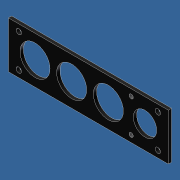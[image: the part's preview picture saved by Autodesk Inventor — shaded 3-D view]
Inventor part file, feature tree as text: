
AUTODESK INVENTOR PART (.ipt)
format: ipt  version: unknown  size: 224,256 bytes
history: native  units: in
note: dims shown in document units (in); Inventor stores cm internally (conversion verified against a paired STEP export)
features: sketch x5, extrude x3, hole x2, reference x2
ambient origin geometry x8: Origin, YZ Plane, XZ Plane, XY Plane, X Axis, Y Axis, Z Axis, Center Point
bodies: Solid1 (feature_tree)
feature tree (12):
  extrude  "Extrusion1"  Depth=1.75in
  extrude  "Extrusion2"  Depth=1.125in
  hole  "Hole1"  [1 undecoded]
  hole  "Hole2"  [1 undecoded]
  extrude  "Extrusion3"  Depth=0.25in
  sketch  "Sketch1"  dims[d0=6.0in d1=1.75in]
  sketch  "Sketch2"  dims[d2=0.125in d3=0.0in d4=1.125in]
  sketch  "Sketch3"  dims[d5=2.375in d6=0.875in]
  sketch  "Sketch4"  dims[d7=0.125in d8=0.0in d9=0.3937in]
  reference  "Reference1"
  reference  "Reference2"
  sketch  "Sketch5"  dims[d10=0.3937in d11=0.25in d12=0.25in d13=0.3937in d14=0.3937in d15=0.25in d16=0.25in d17=0.201in d18=0.75in d19=0.385in d20=0.25in d21=0.5635in d22=1.0in d23=0.8108in d24=0.156in d25=0.75in d26=0.375in d27=0.25in d28=0.5635in d29=1.0in d30=0.8108in d31=1.125in d32=0.875in d33=1.0in d34=1.125in d35=1.375in d36=0.875in d37=0.875in d38=0.875in d39=0.875in d40=1.0in d41=0.0in]
note: 2 required parameter values undecoded (feature->parameter linkage not recoverable at this tier; creation-order binding heuristic only, values carry confidence <= 0.55)
